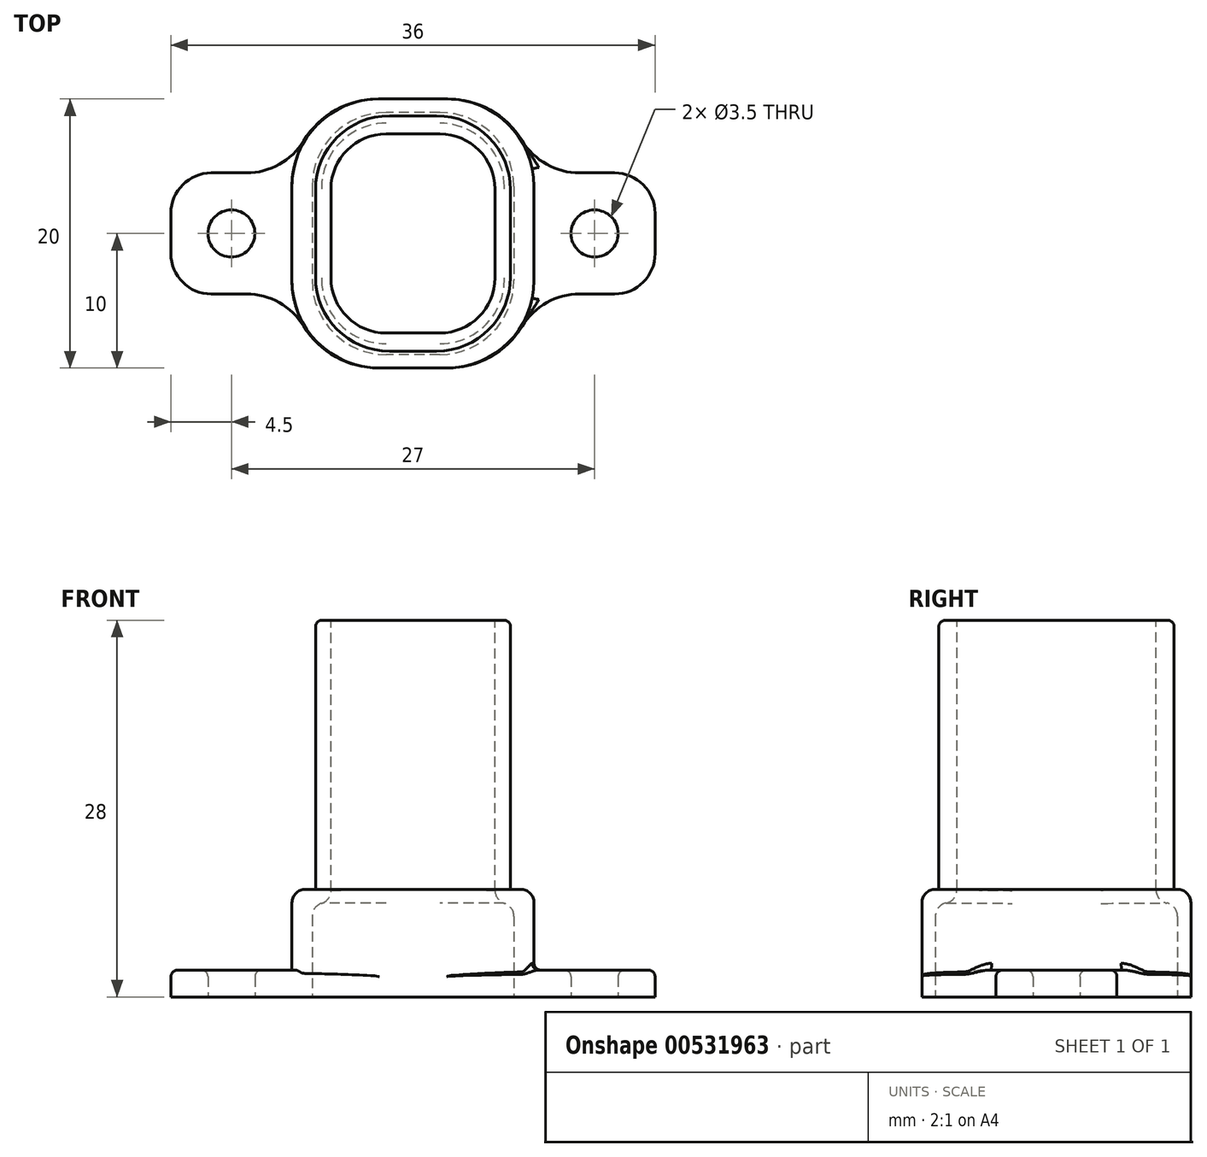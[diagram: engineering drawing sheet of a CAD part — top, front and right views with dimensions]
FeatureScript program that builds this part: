
annotation { "Feature Type Name" : "Feature", "Feature Type Description" : "" }
export const myFeature = defineFeature(function(context is Context, id is Id, definition is map)
    precondition{}
    {
        {
            var Q0;
            Q0=qCreatedBy(makeId("Top.planeOp"),FACE);
            var sketch = newSketch(context, id + "F0", { "sketchPlane" : qUnion([Q0])});
            skLineSegment(sketch, "E0", {"start": v(0, 10) * mm, "end": v(2.58, 10) * mm});
            skLineSegment(sketch, "E1", {"start": v(9, 4.5) * mm, "end": v(15, 4.5) * mm});
            skLineSegment(sketch, "E2.MirrorCS", {"start": v(0, -10) * mm, "end": v(2.58, -10) * mm});
            skPoint(sketch, "E3.visualSharp", {"position": v(9, -10) * mm});
            skArc(sketch, "E3.filletArc", {"start": v(2.58, -10) * mm, "mid": v(6.8, -8.44) * mm, "end": v(9, -4.5) * mm});
            skPoint(sketch, "E4.visualSharp", {"position": v(9, 10) * mm});
            skArc(sketch, "E4.filletArc", {"start": v(9, 4.5) * mm, "mid": v(6.8, 8.44) * mm, "end": v(2.58, 10) * mm});
            skCircle(sketch, "E5", {"center": v(13.5, 0) * mm, "radius": 1.75 * mm});
            skLineSegment(sketch, "E6.MirrorCS", {"start": v(-9, -4.5) * mm, "end": v(-9, -4.5) * mm});
            skArc(sketch, "E7.MirrorCS", {"start": v(-9, 4.5) * mm, "mid": v(-6.8, 8.44) * mm, "end": v(-2.58, 10) * mm});
            skArc(sketch, "E8.MirrorCS", {"start": v(-2.58, -10) * mm, "mid": v(-6.8, -8.44) * mm, "end": v(-9, -4.5) * mm});
            skPoint(sketch, "E9.MirrorP", {"position": v(-9, 10) * mm});
            skCircle(sketch, "E10.MirrorC", {"center": v(-13.5, 0) * mm, "radius": 1.75 * mm});
            skLineSegment(sketch, "E11.MirrorCS", {"start": v(0, 10) * mm, "end": v(-2.58, 10) * mm});
            skPoint(sketch, "E12.MirrorP", {"position": v(-9, -10) * mm});
            skLineSegment(sketch, "E13.MirrorCS", {"start": v(0, -10) * mm, "end": v(-2.58, -10) * mm});
            skLineSegment(sketch, "E14", {"start": v(9, 4.5) * mm, "end": v(9, 4.5) * mm});
            skLineSegment(sketch, "E15.MirrorCS", {"start": v(9, -4.5) * mm, "end": v(15, -4.5) * mm});
            skLineSegment(sketch, "E16.MirrorCS", {"start": v(-9, -4.5) * mm, "end": v(-15, -4.5) * mm});
            skLineSegment(sketch, "E17.MirrorCS", {"start": v(-9, 4.5) * mm, "end": v(-9, 4.5) * mm});
            skLineSegment(sketch, "E18.MirrorCS", {"start": v(-9, 4.5) * mm, "end": v(-15, 4.5) * mm});
            skLineSegment(sketch, "E19", {"start": v(18, 1.5) * mm, "end": v(18, -1.5) * mm});
            skLineSegment(sketch, "E20.MirrorCS", {"start": v(-18, 1.5) * mm, "end": v(-18, -1.5) * mm});
            skPoint(sketch, "E21.visualSharp", {"position": v(18, -4.5) * mm});
            skArc(sketch, "E21.filletArc", {"start": v(15, -4.5) * mm, "mid": v(17.12, -3.62) * mm, "end": v(18, -1.5) * mm});
            skPoint(sketch, "E22.visualSharp", {"position": v(18, 4.5) * mm});
            skArc(sketch, "E22.filletArc", {"start": v(18, 1.5) * mm, "mid": v(17.12, 3.62) * mm, "end": v(15, 4.5) * mm});
            skPoint(sketch, "E23.visualSharp", {"position": v(-18, -4.5) * mm});
            skArc(sketch, "E23.filletArc", {"start": v(-18, -1.5) * mm, "mid": v(-17.12, -3.62) * mm, "end": v(-15, -4.5) * mm});
            skPoint(sketch, "E24.visualSharp", {"position": v(-18, 4.5) * mm});
            skArc(sketch, "E24.filletArc", {"start": v(-15, 4.5) * mm, "mid": v(-17.12, 3.62) * mm, "end": v(-18, 1.5) * mm});
            skSolve(sketch);
        }
        {
            var Q0;
            Q0=makeQuery(id+"F0.imprint","IMPRINT",FACE,{"disambiguationData":[TD([[makeQuery(id+"F0.imprint","IMPRINT",EDGE,{"derivedFrom":sQuery(id+"F0.wireOp",EDGE,"E0")}),-1.0]])]});
            extrude(context, id + "F1", {"entities" : qUnion([Q0]), "depth" : 2 * mm});
        }
        {
            var Q0;
            Q0=makeQuery(id+"F1.opExtrude","CAP_FACE",FACE,{"disambiguationData":[OSD([sQuery(id+"F0.wireOp",EDGE,"E0"),sQuery(id+"F0.wireOp",EDGE,"0BcfFEev-HaRZ-5ouv-0YSG-DbNPpO34d7aD"),sQuery(id+"F0.wireOp",EDGE,"E1"),sQuery(id+"F0.wireOp",EDGE,"mw69Gi3L-mCg4-kHwd-bUB8-XadwVNwFAuX0"),sQuery(id+"F0.wireOp",EDGE,"E2.MirrorCS"),sQuery(id+"F0.wireOp",EDGE,"1972dede-b6b3-40a4-a7b3-59cccf1cca880.MirrorCS"),sQuery(id+"F0.wireOp",EDGE,"c089cd60-ec5b-4c1c-bc61-83843cef7b110.MirrorCS"),sQuery(id+"F0.wireOp",EDGE,"5aebf0b1-4e2b-4ef7-8841-31fb83e5fd4e0.MirrorCS"),sQuery(id+"F0.wireOp",EDGE,"e9b68053-2714-4198-8a57-fe7666c67739.filletArc"),sQuery(id+"F0.wireOp",EDGE,"cc1364d8-9746-44fa-80b3-7ab1895dc222.filletArc"),sQuery(id+"F0.wireOp",EDGE,"fe112896-788f-424a-8313-c3a22471cd30.filletArc"),sQuery(id+"F0.wireOp",EDGE,"95379224-ee1b-4c94-bb63-f84c200c6d7f.filletArc"),sQuery(id+"F0.wireOp",EDGE,"E3.filletArc"),sQuery(id+"F0.wireOp",EDGE,"E4.filletArc"),sQuery(id+"F0.wireOp",EDGE,"E5"),sQuery(id+"F0.wireOp",EDGE,"ce60d5c9-9f61-4fa3-81f9-5f5bba9f42aa0.MirrorCS"),sQuery(id+"F0.wireOp",EDGE,"E6.MirrorCS"),sQuery(id+"F0.wireOp",EDGE,"E7.MirrorCS"),sQuery(id+"F0.wireOp",EDGE,"E8.MirrorCS"),sQuery(id+"F0.wireOp",EDGE,"ce60d5c9-9f61-4fa3-81f9-5f5bba9f42aa4.MirrorCS"),sQuery(id+"F0.wireOp",EDGE,"ce60d5c9-9f61-4fa3-81f9-5f5bba9f42aa5.MirrorCS"),sQuery(id+"F0.wireOp",EDGE,"ce60d5c9-9f61-4fa3-81f9-5f5bba9f42aa6.MirrorCS"),sQuery(id+"F0.wireOp",EDGE,"ce60d5c9-9f61-4fa3-81f9-5f5bba9f42aa7.MirrorCS"),sQuery(id+"F0.wireOp",EDGE,"E10.MirrorC"),sQuery(id+"F0.wireOp",EDGE,"E11.MirrorCS"),sQuery(id+"F0.wireOp",EDGE,"E64.MirrorCS"),sQuery(id+"F0.wireOp",EDGE,"E65.MirrorCS"),sQuery(id+"F0.wireOp",EDGE,"E66.MirrorCS"),sQuery(id+"F0.wireOp",EDGE,"E13.MirrorCS"),sQuery(id+"F0.wireOp",EDGE,"E70.MirrorCS")])],"isStart":false});
            var sketch = newSketch(context, id + "F2", { "sketchPlane" : qUnion([Q0])});
            skLineSegment(sketch, "E25.bottom", {"start": v(2.5, -10) * mm, "end": v(-2.5, -10) * mm});
            skLineSegment(sketch, "E25.top", {"start": v(2.5, 10) * mm, "end": v(-2.5, 10) * mm});
            skLineSegment(sketch, "E25.left", {"start": v(9, -3.5) * mm, "end": v(9, 3.5) * mm});
            skLineSegment(sketch, "E25.right", {"start": v(-9, -3.5) * mm, "end": v(-9, 3.5) * mm});
            skPoint(sketch, "E25.middle", {"position": v(0, 0) * mm});
            skPoint(sketch, "E26.visualSharp", {"position": v(-9, 10) * mm});
            skArc(sketch, "E26.filletArc", {"start": v(-2.5, 10) * mm, "mid": v(-7.1, 8.1) * mm, "end": v(-9, 3.5) * mm});
            skPoint(sketch, "E27.visualSharp", {"position": v(9, 10) * mm});
            skArc(sketch, "E27.filletArc", {"start": v(9, 3.5) * mm, "mid": v(7.1, 8.1) * mm, "end": v(2.5, 10) * mm});
            skPoint(sketch, "E28.visualSharp", {"position": v(9, -10) * mm});
            skArc(sketch, "E28.filletArc", {"start": v(2.5, -10) * mm, "mid": v(7.1, -8.1) * mm, "end": v(9, -3.5) * mm});
            skPoint(sketch, "E29.visualSharp", {"position": v(-9, -10) * mm});
            skArc(sketch, "E29.filletArc", {"start": v(-9, -3.5) * mm, "mid": v(-7.1, -8.1) * mm, "end": v(-2.5, -10) * mm});
            skSolve(sketch);
        }
        {
            var Q0;
            Q0=qSketchRegion(id+"F2",true);
            extrude(context, id + "F3", {"entities" : qUnion([Q0]), "operationType" : NewBodyOperationType.ADD, "depth" : 6 * mm, "offsetDistance" : 25 * mm});
        }
        {
            var Q0;
            Q0=makeQuery(id+"F3.opExtrude","CAP_FACE",FACE,{"disambiguationData":[OSD([sQuery(id+"F2.wireOp",EDGE,"E25.bottom"),sQuery(id+"F2.wireOp",EDGE,"E25.top"),sQuery(id+"F2.wireOp",EDGE,"E25.left"),sQuery(id+"F2.wireOp",EDGE,"E25.right"),sQuery(id+"F2.wireOp",EDGE,"E26.filletArc"),sQuery(id+"F2.wireOp",EDGE,"E27.filletArc"),sQuery(id+"F2.wireOp",EDGE,"E28.filletArc"),sQuery(id+"F2.wireOp",EDGE,"E29.filletArc")])],"isStart":false});
            var sketch = newSketch(context, id + "F4", { "sketchPlane" : qUnion([Q0])});
            skLineSegment(sketch, "E30.bottom", {"start": v(1.75, -8.75) * mm, "end": v(-1.75, -8.75) * mm});
            skLineSegment(sketch, "E30.top", {"start": v(1.75, 8.75) * mm, "end": v(-1.75, 8.75) * mm});
            skLineSegment(sketch, "E30.left", {"start": v(7.25, -3.25) * mm, "end": v(7.25, 3.25) * mm});
            skLineSegment(sketch, "E30.right", {"start": v(-7.25, -3.25) * mm, "end": v(-7.25, 3.25) * mm});
            skPoint(sketch, "E30.middle", {"position": v(0, 0) * mm});
            skPoint(sketch, "E31.visualSharp", {"position": v(-7.25, 8.75) * mm});
            skArc(sketch, "E31.filletArc", {"start": v(-1.75, 8.75) * mm, "mid": v(-5.64, 7.14) * mm, "end": v(-7.25, 3.25) * mm});
            skPoint(sketch, "E32.visualSharp", {"position": v(7.25, 8.75) * mm});
            skArc(sketch, "E33.filletArc", {"start": v(7.25, 3.25) * mm, "mid": v(5.64, 7.14) * mm, "end": v(1.75, 8.75) * mm});
            skPoint(sketch, "E34.visualSharp", {"position": v(7.25, -8.75) * mm});
            skArc(sketch, "E34.filletArc", {"start": v(1.75, -8.75) * mm, "mid": v(5.64, -7.14) * mm, "end": v(7.25, -3.25) * mm});
            skPoint(sketch, "E35.visualSharp", {"position": v(-7.25, -8.75) * mm});
            skArc(sketch, "E35.filletArc", {"start": v(-7.25, -3.25) * mm, "mid": v(-5.64, -7.14) * mm, "end": v(-1.75, -8.75) * mm});
            skSolve(sketch);
        }
        {
            var Q0;
            Q0=makeQuery(id+"F4.imprint","IMPRINT",FACE,{"disambiguationData":[TD([[makeQuery(id+"F4.imprint","IMPRINT",EDGE,{"derivedFrom":sQuery(id+"F4.wireOp",EDGE,"E30.bottom")}),-1.0]])]});
            extrude(context, id + "F5", {"entities" : qUnion([Q0]), "operationType" : NewBodyOperationType.ADD, "depth" : 20 * mm});
        }
        {
            var Q0;
            Q0=makeQuery(id+"F5.opExtrude","CAP_FACE",FACE,{"disambiguationData":[OSD([sQuery(id+"F4.wireOp",EDGE,"E30.bottom"),sQuery(id+"F4.wireOp",EDGE,"E30.top"),sQuery(id+"F4.wireOp",EDGE,"E30.left"),sQuery(id+"F4.wireOp",EDGE,"E30.right"),sQuery(id+"F4.wireOp",EDGE,"E31.filletArc"),sQuery(id+"F4.wireOp",EDGE,"E33.filletArc"),sQuery(id+"F4.wireOp",EDGE,"E34.filletArc"),sQuery(id+"F4.wireOp",EDGE,"E35.filletArc")])],"isStart":false});
            var sketch = newSketch(context, id + "F6", { "sketchPlane" : qUnion([Q0])});
            skLineSegment(sketch, "E36.bottom", {"start": v(2, -7.4) * mm, "end": v(-2, -7.4) * mm});
            skLineSegment(sketch, "E36.top", {"start": v(2, 7.4) * mm, "end": v(-2, 7.4) * mm});
            skLineSegment(sketch, "E36.left", {"start": v(6.1, -3.3) * mm, "end": v(6.1, 3.3) * mm});
            skLineSegment(sketch, "E36.right", {"start": v(-6.1, -3.3) * mm, "end": v(-6.1, 3.3) * mm});
            skPoint(sketch, "E36.middle", {"position": v(0, 0) * mm});
            skPoint(sketch, "E37.visualSharp", {"position": v(-6.1, 7.4) * mm});
            skArc(sketch, "E37.filletArc", {"start": v(-2, 7.4) * mm, "mid": v(-4.9, 6.2) * mm, "end": v(-6.1, 3.3) * mm});
            skPoint(sketch, "E38.visualSharp", {"position": v(6.1, 7.4) * mm});
            skArc(sketch, "E38.filletArc", {"start": v(6.1, 3.3) * mm, "mid": v(4.9, 6.2) * mm, "end": v(2, 7.4) * mm});
            skPoint(sketch, "E39.visualSharp", {"position": v(6.1, -7.4) * mm});
            skArc(sketch, "E39.filletArc", {"start": v(2, -7.4) * mm, "mid": v(4.9, -6.2) * mm, "end": v(6.1, -3.3) * mm});
            skPoint(sketch, "E40.visualSharp", {"position": v(-6.1, -7.4) * mm});
            skArc(sketch, "E40.filletArc", {"start": v(-6.1, -3.3) * mm, "mid": v(-4.9, -6.2) * mm, "end": v(-2, -7.4) * mm});
            skSolve(sketch);
        }
        {
            var Q0;
            Q0=qSketchRegion(id+"F6",true);
            extrude(context, id + "F7", {"entities" : qUnion([Q0]), "operationType" : NewBodyOperationType.REMOVE, "oppositeDirection" : true, "depth" : 30 * mm});
        }
        {
            var Q0;
            Q0=makeQuery(id+"F1.opExtrude","CAP_FACE",FACE,{"disambiguationData":[OSD([sQuery(id+"F0.wireOp",EDGE,"E0"),sQuery(id+"F0.wireOp",EDGE,"0BcfFEev-HaRZ-5ouv-0YSG-DbNPpO34d7aD"),sQuery(id+"F0.wireOp",EDGE,"E1"),sQuery(id+"F0.wireOp",EDGE,"mw69Gi3L-mCg4-kHwd-bUB8-XadwVNwFAuX0"),sQuery(id+"F0.wireOp",EDGE,"E2.MirrorCS"),sQuery(id+"F0.wireOp",EDGE,"1972dede-b6b3-40a4-a7b3-59cccf1cca880.MirrorCS"),sQuery(id+"F0.wireOp",EDGE,"c089cd60-ec5b-4c1c-bc61-83843cef7b110.MirrorCS"),sQuery(id+"F0.wireOp",EDGE,"5aebf0b1-4e2b-4ef7-8841-31fb83e5fd4e0.MirrorCS"),sQuery(id+"F0.wireOp",EDGE,"e9b68053-2714-4198-8a57-fe7666c67739.filletArc"),sQuery(id+"F0.wireOp",EDGE,"cc1364d8-9746-44fa-80b3-7ab1895dc222.filletArc"),sQuery(id+"F0.wireOp",EDGE,"fe112896-788f-424a-8313-c3a22471cd30.filletArc"),sQuery(id+"F0.wireOp",EDGE,"95379224-ee1b-4c94-bb63-f84c200c6d7f.filletArc"),sQuery(id+"F0.wireOp",EDGE,"E3.filletArc"),sQuery(id+"F0.wireOp",EDGE,"E4.filletArc"),sQuery(id+"F0.wireOp",EDGE,"E5"),sQuery(id+"F0.wireOp",EDGE,"ce60d5c9-9f61-4fa3-81f9-5f5bba9f42aa0.MirrorCS"),sQuery(id+"F0.wireOp",EDGE,"E6.MirrorCS"),sQuery(id+"F0.wireOp",EDGE,"E7.MirrorCS"),sQuery(id+"F0.wireOp",EDGE,"E8.MirrorCS"),sQuery(id+"F0.wireOp",EDGE,"ce60d5c9-9f61-4fa3-81f9-5f5bba9f42aa4.MirrorCS"),sQuery(id+"F0.wireOp",EDGE,"ce60d5c9-9f61-4fa3-81f9-5f5bba9f42aa5.MirrorCS"),sQuery(id+"F0.wireOp",EDGE,"ce60d5c9-9f61-4fa3-81f9-5f5bba9f42aa6.MirrorCS"),sQuery(id+"F0.wireOp",EDGE,"ce60d5c9-9f61-4fa3-81f9-5f5bba9f42aa7.MirrorCS"),sQuery(id+"F0.wireOp",EDGE,"E10.MirrorC"),sQuery(id+"F0.wireOp",EDGE,"E11.MirrorCS"),sQuery(id+"F0.wireOp",EDGE,"E64.MirrorCS"),sQuery(id+"F0.wireOp",EDGE,"E65.MirrorCS"),sQuery(id+"F0.wireOp",EDGE,"E66.MirrorCS"),sQuery(id+"F0.wireOp",EDGE,"E13.MirrorCS"),sQuery(id+"F0.wireOp",EDGE,"E70.MirrorCS")])],"isStart":true});
            var sketch = newSketch(context, id + "F8", { "sketchPlane" : qUnion([Q0])});
            skLineSegment(sketch, "E41.bottom", {"start": v(2, -9) * mm, "end": v(-2, -9) * mm});
            skLineSegment(sketch, "E41.top", {"start": v(2, 9) * mm, "end": v(-2, 9) * mm});
            skLineSegment(sketch, "E41.left", {"start": v(7.5, -3.5) * mm, "end": v(7.5, 3.5) * mm});
            skLineSegment(sketch, "E41.right", {"start": v(-7.5, -3.5) * mm, "end": v(-7.5, 3.5) * mm});
            skPoint(sketch, "E41.middle", {"position": v(0, 0) * mm});
            skPoint(sketch, "E42.visualSharp", {"position": v(-7.5, 9) * mm});
            skArc(sketch, "E42.filletArc", {"start": v(-2, 9) * mm, "mid": v(-5.89, 7.39) * mm, "end": v(-7.5, 3.5) * mm});
            skPoint(sketch, "E43.visualSharp", {"position": v(7.5, 9) * mm});
            skArc(sketch, "E43.filletArc", {"start": v(7.5, 3.5) * mm, "mid": v(5.89, 7.39) * mm, "end": v(2, 9) * mm});
            skPoint(sketch, "E44.visualSharp", {"position": v(7.5, -9) * mm});
            skArc(sketch, "E44.filletArc", {"start": v(2, -9) * mm, "mid": v(5.89, -7.39) * mm, "end": v(7.5, -3.5) * mm});
            skPoint(sketch, "E45.visualSharp", {"position": v(-7.5, -9) * mm});
            skArc(sketch, "E45.filletArc", {"start": v(-7.5, -3.5) * mm, "mid": v(-5.89, -7.39) * mm, "end": v(-2, -9) * mm});
            skSolve(sketch);
        }
        {
            var Q0;
            Q0=qSketchRegion(id+"F8",true);
            extrude(context, id + "F9", {"entities" : qUnion([Q0]), "operationType" : NewBodyOperationType.REMOVE, "oppositeDirection" : true, "depth" : 7 * mm, "offsetDistance" : 25 * mm});
        }
        {
            var Q0;
            Q0=makeQuery(id+"F9.boolean.opBoolean","COPY",EDGE,{"derivedFrom":makeQuery(id+"F9.opExtrude","CAP_EDGE",EDGE,{"disambiguationData":[OSD([sQuery(id+"F8.wireOp",EDGE,"E45.filletArc")])],"isStart":false})});
            var Q1;
            Q1=makeQuery(id+"F5.opExtrude","CAP_EDGE",EDGE,{"disambiguationData":[OSD([sQuery(id+"F4.wireOp",EDGE,"E30.left")])],"isStart":true});
            fillet(context, id + "F10", {"entities" : qUnion([Q0, Q1]), "radius" : 1 * mm, "tangentPropagation" : true, "allowEdgeOverflow" : false});
        }
        {
            var Q0;
            Q0=makeQuery(id+"F3.opExtrude","CAP_EDGE",EDGE,{"disambiguationData":[OSD([sQuery(id+"F2.wireOp",EDGE,"E27.filletArc")])],"isStart":false});
            fillet(context, id + "F11", {"entities" : qUnion([Q0]), "radius" : 1 * mm, "tangentPropagation" : true, "allowEdgeOverflow" : false});
        }
        {
            var Q0;
            Q0=makeQuery(id+"F9.boolean.opBoolean","INTERSECT",EDGE,{"derivedFrom":[makeQuery(id+"F7.boolean.opBoolean","COPY",FACE,{"derivedFrom":makeQuery(id+"F7.opExtrude","SWEPT_FACE",FACE,{"disambiguationData":[OSD([sQuery(id+"F6.wireOp",EDGE,"E38.filletArc")])]})}),makeQuery(id+"F9.opExtrude","CAP_FACE",FACE,{"disambiguationData":[OSD([sQuery(id+"F8.wireOp",EDGE,"E41.bottom"),sQuery(id+"F8.wireOp",EDGE,"E41.top"),sQuery(id+"F8.wireOp",EDGE,"E41.left"),sQuery(id+"F8.wireOp",EDGE,"E41.right"),sQuery(id+"F8.wireOp",EDGE,"E42.filletArc"),sQuery(id+"F8.wireOp",EDGE,"E43.filletArc"),sQuery(id+"F8.wireOp",EDGE,"E44.filletArc"),sQuery(id+"F8.wireOp",EDGE,"E45.filletArc")])],"isStart":false})]});
            fillet(context, id + "F12", {"entities" : qUnion([Q0]), "radius" : 1 * mm, "tangentPropagation" : true, "allowEdgeOverflow" : false});
        }
        {
            var Q0;
            Q0=makeQuery(id+"F1.opExtrude","SWEPT_EDGE",EDGE,{"disambiguationData":[OSD([sQuery(id+"F0.wireOp",EDGE,"E7.MirrorCS"),sQuery(id+"F0.wireOp",EDGE,"E18.MirrorCS")])]});
            var Q1;
            Q1=makeQuery(id+"F1.opExtrude","SWEPT_EDGE",EDGE,{"disambiguationData":[OSD([sQuery(id+"F0.wireOp",EDGE,"E1"),sQuery(id+"F0.wireOp",EDGE,"E4.filletArc")])]});
            var Q2;
            Q2=makeQuery(id+"F1.opExtrude","SWEPT_EDGE",EDGE,{"disambiguationData":[OSD([sQuery(id+"F0.wireOp",EDGE,"E3.filletArc"),sQuery(id+"F0.wireOp",EDGE,"E15.MirrorCS")])]});
            var Q3;
            Q3=makeQuery(id+"F1.opExtrude","SWEPT_EDGE",EDGE,{"disambiguationData":[OSD([sQuery(id+"F0.wireOp",EDGE,"E8.MirrorCS"),sQuery(id+"F0.wireOp",EDGE,"E16.MirrorCS")])]});
            fillet(context, id + "F13", {"entities" : qUnion([Q0, Q1, Q2, Q3]), "radius" : 5 * mm, "tangentPropagation" : true, "allowEdgeOverflow" : false});
        }
        {
            var Q0;
            Q0=makeQuery(id+"F1.opExtrude","CAP_EDGE",EDGE,{"disambiguationData":[OSD([sQuery(id+"F0.wireOp",EDGE,"E24.filletArc")])],"isStart":false});
            var Q1;
            Q1=makeQuery(id+"F1.opExtrude","CAP_EDGE",EDGE,{"disambiguationData":[OSD([sQuery(id+"F0.wireOp",EDGE,"E22.filletArc")])],"isStart":false});
            var Q2;
            Q2=makeQuery(id+"F1.opExtrude","CAP_EDGE",EDGE,{"disambiguationData":[OSD([sQuery(id+"F0.wireOp",EDGE,"E5")])],"isStart":false});
            var Q3;
            Q3=makeQuery(id+"F1.opExtrude","CAP_EDGE",EDGE,{"disambiguationData":[OSD([sQuery(id+"F0.wireOp",EDGE,"E10.MirrorC")])],"isStart":false});
            fillet(context, id + "F14", {"entities" : qUnion([Q0, Q1, Q2, Q3]), "radius" : 0.5 * mm, "tangentPropagation" : true, "allowEdgeOverflow" : false});
        }
        {
            var Q0;
            Q0=makeQuery(id+"F3.opExtrude","CAP_EDGE",EDGE,{"disambiguationData":[OSD([sQuery(id+"F2.wireOp",EDGE,"E25.left")])],"isStart":true});
            var Q1;
            Q1=makeQuery(id+"F3.boolean.opBoolean","SPLIT",EDGE,{"derivedFrom":makeQuery(id+"F3.opExtrude","CAP_EDGE",EDGE,{"disambiguationData":[OSD([sQuery(id+"F2.wireOp",EDGE,"E26.filletArc")])],"isStart":true})});
            var Q2;
            Q2=makeQuery(id+"F5.opExtrude","CAP_EDGE",EDGE,{"disambiguationData":[OSD([sQuery(id+"F4.wireOp",EDGE,"E31.filletArc")])],"isStart":false});
            var Q3;
            Q3=makeQuery(id+"F7.boolean.opBoolean","COPY",EDGE,{"derivedFrom":makeQuery(id+"F7.opExtrude","CAP_EDGE",EDGE,{"disambiguationData":[OSD([sQuery(id+"F6.wireOp",EDGE,"E37.filletArc")])],"isStart":true})});
            fillet(context, id + "F15", {"entities" : qUnion([Q0, Q1, Q2, Q3]), "radius" : 0.5 * mm, "tangentPropagation" : true, "allowEdgeOverflow" : false});
        }
    });
